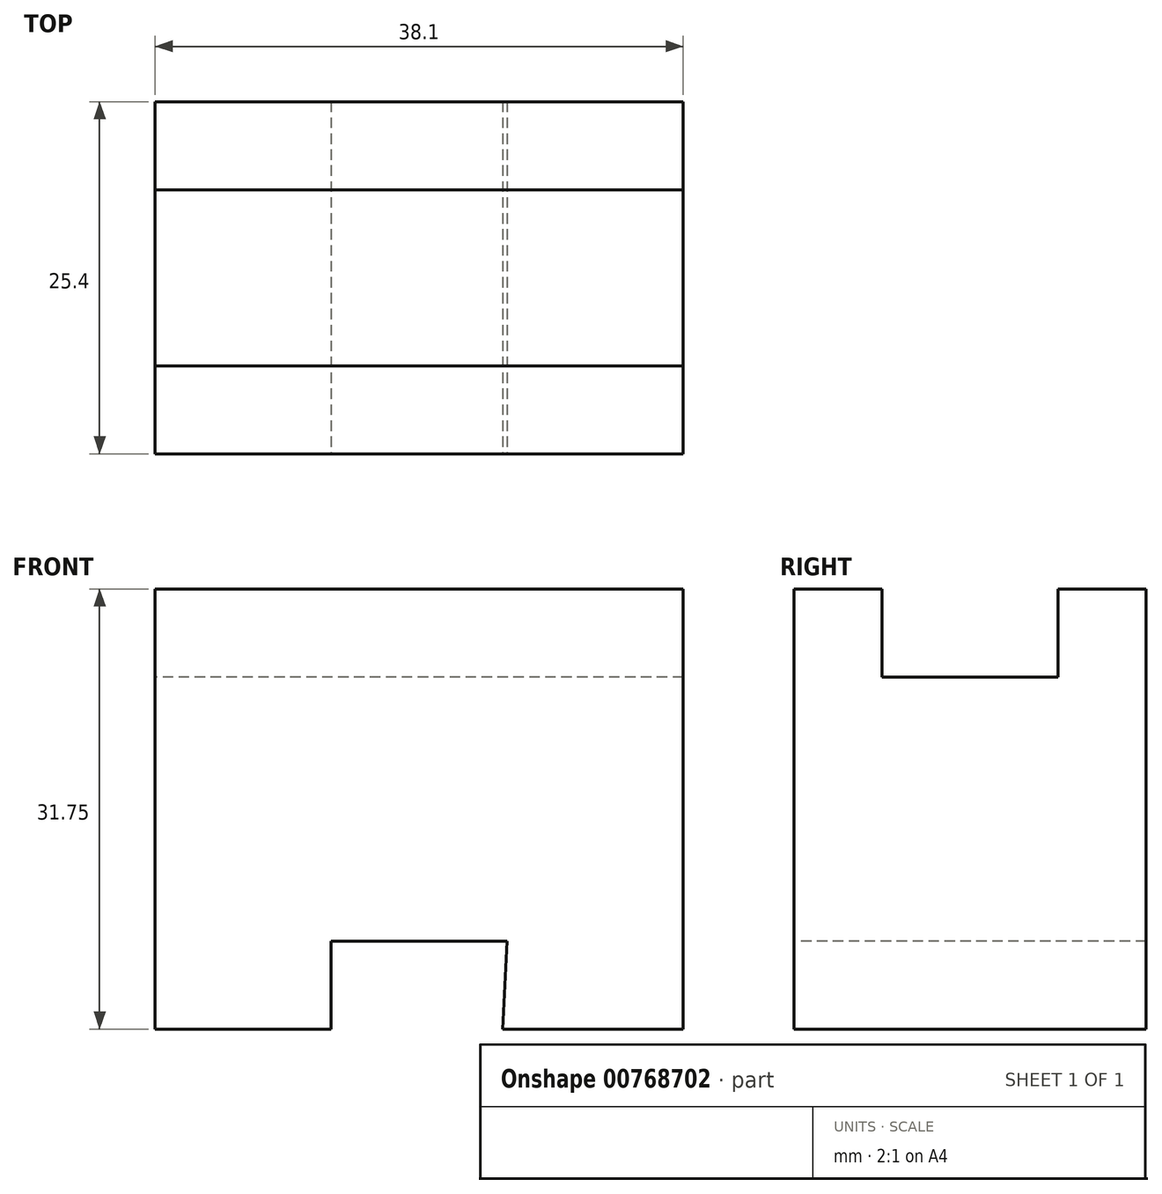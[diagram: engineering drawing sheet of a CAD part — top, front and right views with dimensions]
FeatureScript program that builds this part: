
annotation { "Feature Type Name" : "Feature", "Feature Type Description" : "" }
export const myFeature = defineFeature(function(context is Context, id is Id, definition is map)
    precondition{}
    {
        {
            var Q0;
            Q0=qCreatedBy(makeId("Right.planeOp"),FACE);
            var sketch = newSketch(context, id + "F0", { "sketchPlane" : qUnion([Q0])});
            skLineSegment(sketch, "E0", {"start": v(0, 0) * mm, "end": v(25.4, 0) * mm});
            skLineSegment(sketch, "E1", {"start": v(25.4, 0) * mm, "end": v(25.4, 31.75) * mm});
            skLineSegment(sketch, "E2", {"start": v(25.4, 31.75) * mm, "end": v(19.05, 31.75) * mm});
            skLineSegment(sketch, "E3", {"start": v(19.05, 31.75) * mm, "end": v(19.05, 25.4) * mm});
            skLineSegment(sketch, "E4", {"start": v(19.05, 25.4) * mm, "end": v(6.35, 25.4) * mm});
            skLineSegment(sketch, "E5", {"start": v(6.35, 25.4) * mm, "end": v(6.35, 31.75) * mm});
            skLineSegment(sketch, "E6", {"start": v(6.35, 31.75) * mm, "end": v(0, 31.75) * mm});
            skLineSegment(sketch, "E7", {"start": v(0, 31.75) * mm, "end": v(0, 0) * mm});
            skSolve(sketch);
        }
        {
            var Q0;
            Q0 = qSketchRegion(id + "F0", true);
            extrude(context, id + "F1", {"entities" : qUnion([Q0]), "depth" : 38.1 * mm, "offsetDistance" : 25.4 * mm});
        }
        {
            var Q0;
            Q0=makeQuery(id+"F1.opExtrude","SWEPT_FACE",FACE,{"disambiguationData":[OSD([sQuery(id+"F0.wireOp",EDGE,"E7")])]});
            var sketch = newSketch(context, id + "F2", { "sketchPlane" : qUnion([Q0])});
            skLineSegment(sketch, "E8", {"start": v(0, 0) * mm, "end": v(12.7, 0) * mm});
            skLineSegment(sketch, "E9", {"start": v(12.7, 0) * mm, "end": v(12.7, 6.35) * mm});
            skLineSegment(sketch, "E10", {"start": v(12.7, 6.35) * mm, "end": v(25.4, 6.35) * mm});
            skLineSegment(sketch, "E11", {"start": v(25.4, 6.35) * mm, "end": v(25.06, 0) * mm});
            skSolve(sketch);
        }
        {
            var Q0;
            {var subQ0=sQuery(id+"F2.wireOp",EDGE,"E9");Q0=makeQuery(id+"F2.imprint","IMPRINT",FACE,{"disambiguationData":[TD([[makeQuery(id+"F2.imprint","IMPRINT",EDGE,{"derivedFrom":subQ0}),-1.0]])]});}
            extrude(context, id + "F3", {"entities" : qUnion([Q0]), "operationType" : NewBodyOperationType.REMOVE, "endBound" : BoundingType.UP_TO_NEXT, "oppositeDirection" : true, "depth" : 25.4 * mm, "offsetDistance" : 25.4 * mm});
        }
    });
